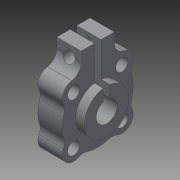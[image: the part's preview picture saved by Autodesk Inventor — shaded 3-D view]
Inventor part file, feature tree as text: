
AUTODESK INVENTOR PART (.ipt)
format: ipt  version: 2014 SP1 (Build 180222100, 222)  size: 219,136 bytes
history: native  units: in
note: dims shown in document units (in); Inventor stores cm internally (conversion verified against a paired STEP export)
features: other x3, sketch x3
ambient origin geometry x8: Origin, YZ Plane, XZ Plane, XY Plane, X Axis, Y Axis, Z Axis, Center Point
bodies: Solid1 (feature_tree)
feature tree (6):
  other  "Clamping Hub.ipt"
  other  "Solid1::Clamping Hub.ipt"
  other  "TaggingFeature1"
  sketch  "Sketch1"  dims[d0=0.3937in]
  sketch  "Sketch2"  dims[d1=0.8in d4=0.77in d6=0.138in d7=0.138in d8=0.138in d9=0.138in d11=0.2362in d12=1.035in d16=0.0375in d17=0.038in d18=0.125in d19=0.125in d20=0.275in d21=0.0in d22=0.5in d23=0.1in d24=0.0in d25=0.138in d26=1.1625in d27=0.0in d32=0.01in]
  sketch  "Sketch3"
